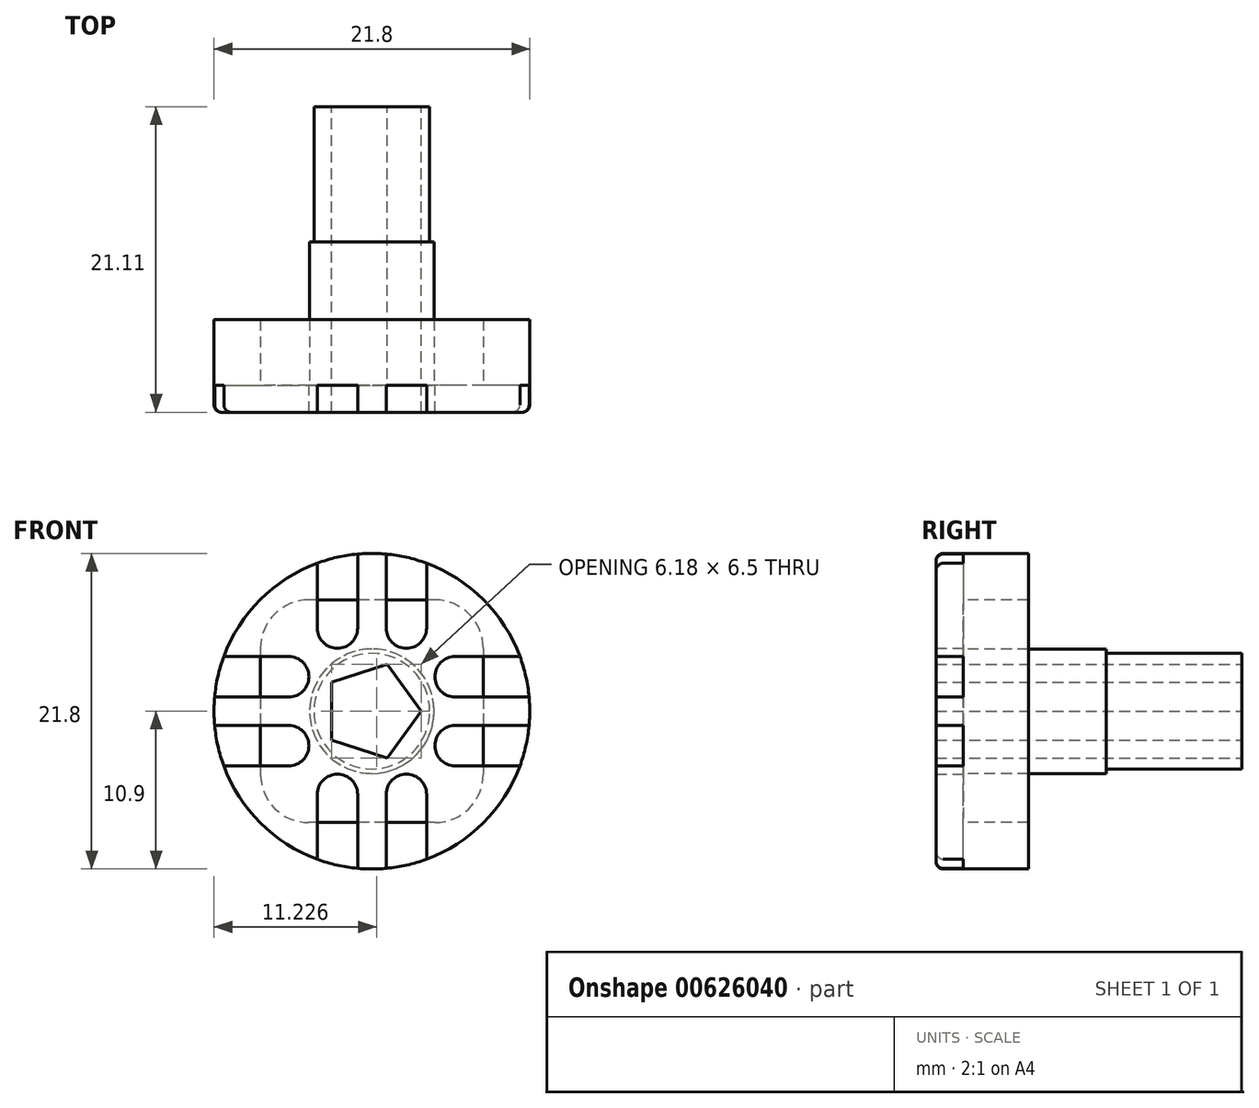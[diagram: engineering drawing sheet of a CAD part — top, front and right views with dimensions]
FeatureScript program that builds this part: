
annotation { "Feature Type Name" : "Feature", "Feature Type Description" : "" }
export const myFeature = defineFeature(function(context is Context, id is Id, definition is map)
    precondition{}
    {
        {
            var Q0;
            Q0=qCreatedBy(makeId("Front.planeOp"),FACE);
            var sketch = newSketch(context, id + "F0", { "sketchPlane" : qUnion([Q0])});
            skCircle(sketch, "E0", {"center": v(0, 0) * mm, "radius": 10.9 * mm});
            skLineSegment(sketch, "E1", {"start": v(-3.77, 10.23) * mm, "end": v(-3.77, 5.75) * mm});
            skLineSegment(sketch, "E2", {"start": v(-0.98, 10.86) * mm, "end": v(-0.98, 5.75) * mm});
            skLineSegment(sketch, "E3", {"start": v(0.99, 10.86) * mm, "end": v(0.99, 5.75) * mm});
            skLineSegment(sketch, "E4", {"start": v(3.78, 10.23) * mm, "end": v(3.78, 5.75) * mm});
            skLineSegment(sketch, "E5", {"start": v(-3.78, -10.23) * mm, "end": v(-3.78, -5.74) * mm});
            skLineSegment(sketch, "E6", {"start": v(-0.99, -10.86) * mm, "end": v(-0.99, -5.74) * mm});
            skLineSegment(sketch, "E7", {"start": v(0.99, -10.86) * mm, "end": v(0.99, -5.74) * mm});
            skLineSegment(sketch, "E8", {"start": v(3.78, -10.23) * mm, "end": v(3.78, -5.74) * mm});
            skLineSegment(sketch, "E9", {"start": v(10.23, -3.78) * mm, "end": v(5.75, -3.78) * mm});
            skLineSegment(sketch, "E10", {"start": v(10.23, 3.78) * mm, "end": v(5.75, 3.78) * mm});
            skLineSegment(sketch, "E11", {"start": v(10.86, 0.99) * mm, "end": v(5.75, 0.99) * mm});
            skLineSegment(sketch, "E12", {"start": v(10.86, -0.99) * mm, "end": v(5.75, -0.99) * mm});
            skLineSegment(sketch, "E13", {"start": v(-10.23, 3.78) * mm, "end": v(-5.75, 3.78) * mm});
            skLineSegment(sketch, "E14", {"start": v(-10.86, 0.99) * mm, "end": v(-5.75, 0.99) * mm});
            skLineSegment(sketch, "E15", {"start": v(-10.86, -0.98) * mm, "end": v(-5.75, -0.98) * mm});
            skLineSegment(sketch, "E16", {"start": v(-10.23, -3.78) * mm, "end": v(-5.75, -3.78) * mm});
            skLineSegment(sketch, "E17", {"start": v(-5.75, -0.98) * mm, "end": v(-5.75, -3.78) * mm, "construction": true});
            skLineSegment(sketch, "E18", {"start": v(-0.98, 5.75) * mm, "end": v(-3.77, 5.75) * mm, "construction": true});
            skLineSegment(sketch, "E19", {"start": v(-0.99, -5.74) * mm, "end": v(-3.78, -5.74) * mm, "construction": true});
            skLineSegment(sketch, "E20", {"start": v(0.99, -5.74) * mm, "end": v(3.78, -5.74) * mm, "construction": true});
            skLineSegment(sketch, "E21", {"start": v(5.75, -0.99) * mm, "end": v(5.75, -3.78) * mm, "construction": true});
            skLineSegment(sketch, "E22", {"start": v(5.75, 0.99) * mm, "end": v(5.75, 3.78) * mm, "construction": true});
            skLineSegment(sketch, "E23", {"start": v(0.99, 5.75) * mm, "end": v(3.78, 5.75) * mm, "construction": true});
            skLineSegment(sketch, "E24", {"start": v(-5.75, 3.78) * mm, "end": v(-5.75, 0.98) * mm, "construction": true});
            skArc(sketch, "E25", {"start": v(-5.75, -3.78) * mm, "mid": v(-4.35, -2.38) * mm, "end": v(-5.75, -0.98) * mm});
            skArc(sketch, "E26", {"start": v(-5.75, 0.99) * mm, "mid": v(-4.35, 2.38) * mm, "end": v(-5.75, 3.78) * mm});
            skArc(sketch, "E27", {"start": v(3.78, -5.74) * mm, "mid": v(2.38, -4.35) * mm, "end": v(0.99, -5.74) * mm});
            skArc(sketch, "E28", {"start": v(-0.99, -5.74) * mm, "mid": v(-2.38, -4.35) * mm, "end": v(-3.78, -5.74) * mm});
            skArc(sketch, "E29", {"start": v(5.75, 3.78) * mm, "mid": v(4.35, 2.38) * mm, "end": v(5.75, 0.99) * mm});
            skArc(sketch, "E30", {"start": v(5.75, -0.99) * mm, "mid": v(4.35, -2.38) * mm, "end": v(5.75, -3.78) * mm});
            skArc(sketch, "E31", {"start": v(-3.77, 5.75) * mm, "mid": v(-2.38, 4.35) * mm, "end": v(-0.98, 5.75) * mm});
            skArc(sketch, "E32", {"start": v(0.99, 5.75) * mm, "mid": v(2.38, 4.35) * mm, "end": v(3.78, 5.75) * mm});
            skLineSegment(sketch, "E33", {"start": v(-4.35, 2.38) * mm, "end": v(4.35, 2.38) * mm, "construction": true});
            skCircle(sketch, "E34.cCircle", {"center": v(0, 0) * mm, "radius": 2.76 * mm, "construction": true});
            skLineSegment(sketch, "E34.0", {"start": v(-2.76, -2) * mm, "end": v(-2.76, 2) * mm});
            skLineSegment(sketch, "E34.1", {"start": v(-2.76, 2) * mm, "end": v(1.06, 3.25) * mm});
            skLineSegment(sketch, "E34.2", {"start": v(1.06, 3.25) * mm, "end": v(3.42, 0) * mm});
            skLineSegment(sketch, "E34.3", {"start": v(3.42, 0) * mm, "end": v(1.06, -3.25) * mm});
            skLineSegment(sketch, "E34.4", {"start": v(1.06, -3.25) * mm, "end": v(-2.76, -2) * mm});
            skPoint(sketch, "E34.0.midPoint", {"position": v(-2.76, 0) * mm});
            skSolve(sketch);
        }
        {
            var Q0;
            {var subQ12=sQuery(id+"F0.wireOp",EDGE,"E1");Q0=makeQuery(id+"F0.imprint","IMPRINT",FACE,{"disambiguationData":[TD([[makeQuery(id+"F0.imprint","IMPRINT",EDGE,{"derivedFrom":subQ12}),-1.0]])]});}
            extrude(context, id + "F1", {"entities" : qUnion([Q0]), "depth" : 1.87 * mm, "offsetDistance" : 25 * mm});
        }
        {
            var Q0;
            Q0=makeQuery(id+"F1.opExtrude","CAP_FACE",FACE,{"disambiguationData":[OSD([sQuery(id+"F0.wireOp",EDGE,"E0"),sQuery(id+"F0.wireOp",EDGE,"E1"),sQuery(id+"F0.wireOp",EDGE,"E2"),sQuery(id+"F0.wireOp",EDGE,"E3"),sQuery(id+"F0.wireOp",EDGE,"E4"),sQuery(id+"F0.wireOp",EDGE,"E5"),sQuery(id+"F0.wireOp",EDGE,"E6"),sQuery(id+"F0.wireOp",EDGE,"E7"),sQuery(id+"F0.wireOp",EDGE,"E8"),sQuery(id+"F0.wireOp",EDGE,"E9"),sQuery(id+"F0.wireOp",EDGE,"E10"),sQuery(id+"F0.wireOp",EDGE,"E11"),sQuery(id+"F0.wireOp",EDGE,"E12"),sQuery(id+"F0.wireOp",EDGE,"E13"),sQuery(id+"F0.wireOp",EDGE,"E14"),sQuery(id+"F0.wireOp",EDGE,"E15"),sQuery(id+"F0.wireOp",EDGE,"E16"),sQuery(id+"F0.wireOp",EDGE,"E25"),sQuery(id+"F0.wireOp",EDGE,"E26"),sQuery(id+"F0.wireOp",EDGE,"E27"),sQuery(id+"F0.wireOp",EDGE,"E28"),sQuery(id+"F0.wireOp",EDGE,"E29"),sQuery(id+"F0.wireOp",EDGE,"E30"),sQuery(id+"F0.wireOp",EDGE,"E31"),sQuery(id+"F0.wireOp",EDGE,"E32"),sQuery(id+"F0.wireOp",EDGE,"E34.0"),sQuery(id+"F0.wireOp",EDGE,"E34.1"),sQuery(id+"F0.wireOp",EDGE,"E34.2"),sQuery(id+"F0.wireOp",EDGE,"E34.3"),sQuery(id+"F0.wireOp",EDGE,"E34.4")])],"isStart":true});
            var sketch = newSketch(context, id + "F2", { "sketchPlane" : qUnion([Q0])});
            skCircle(sketch, "E35", {"center": v(0, 0) * mm, "radius": 4.3 * mm});
            skSolve(sketch);
        }
        {
            var Q0;
            Q0=makeQuery(id+"F2.imprint","IMPRINT",FACE,{"disambiguationData":[TD([[makeQuery(id+"F2.imprint","IMPRINT",EDGE,{"derivedFrom":sQuery(id+"F2.wireOp",EDGE,"E35")}),1.0]])]});
            extrude(context, id + "F3", {"entities" : qUnion([Q0]), "operationType" : NewBodyOperationType.ADD, "depth" : 9.9 * mm, "offsetDistance" : 25 * mm});
        }
        {
            var Q0;
            Q0=makeQuery(id+"F3.opExtrude","CAP_FACE",FACE,{"disambiguationData":[OSD([sQuery(id+"F0.wireOp",EDGE,"E34.0"),sQuery(id+"F0.wireOp",EDGE,"E34.1"),sQuery(id+"F0.wireOp",EDGE,"E34.2"),sQuery(id+"F0.wireOp",EDGE,"E34.3"),sQuery(id+"F0.wireOp",EDGE,"E34.4"),sQuery(id+"F2.wireOp",EDGE,"E35")])],"isStart":false});
            var sketch = newSketch(context, id + "F4", { "sketchPlane" : qUnion([Q0])});
            skCircle(sketch, "E36", {"center": v(0, 0) * mm, "radius": 4 * mm});
            skSolve(sketch);
        }
        {
            var Q0;
            Q0=makeQuery(id+"F4.imprint","IMPRINT",FACE,{"disambiguationData":[TD([[makeQuery(id+"F4.imprint","IMPRINT",EDGE,{"derivedFrom":sQuery(id+"F4.wireOp",EDGE,"E36")}),1.0]])]});
            extrude(context, id + "F5", {"entities" : qUnion([Q0]), "operationType" : NewBodyOperationType.ADD, "depth" : 9.35 * mm, "offsetDistance" : 25 * mm});
        }
        {
            var Q0;
            Q0=makeQuery(id+"F1.opExtrude","CAP_FACE",FACE,{"disambiguationData":[OSD([sQuery(id+"F0.wireOp",EDGE,"E0"),sQuery(id+"F0.wireOp",EDGE,"E1"),sQuery(id+"F0.wireOp",EDGE,"E2"),sQuery(id+"F0.wireOp",EDGE,"E3"),sQuery(id+"F0.wireOp",EDGE,"E4"),sQuery(id+"F0.wireOp",EDGE,"E5"),sQuery(id+"F0.wireOp",EDGE,"E6"),sQuery(id+"F0.wireOp",EDGE,"E7"),sQuery(id+"F0.wireOp",EDGE,"E8"),sQuery(id+"F0.wireOp",EDGE,"E9"),sQuery(id+"F0.wireOp",EDGE,"E10"),sQuery(id+"F0.wireOp",EDGE,"E11"),sQuery(id+"F0.wireOp",EDGE,"E12"),sQuery(id+"F0.wireOp",EDGE,"E13"),sQuery(id+"F0.wireOp",EDGE,"E14"),sQuery(id+"F0.wireOp",EDGE,"E15"),sQuery(id+"F0.wireOp",EDGE,"E16"),sQuery(id+"F0.wireOp",EDGE,"E25"),sQuery(id+"F0.wireOp",EDGE,"E26"),sQuery(id+"F0.wireOp",EDGE,"E27"),sQuery(id+"F0.wireOp",EDGE,"E28"),sQuery(id+"F0.wireOp",EDGE,"E29"),sQuery(id+"F0.wireOp",EDGE,"E30"),sQuery(id+"F0.wireOp",EDGE,"E31"),sQuery(id+"F0.wireOp",EDGE,"E32"),sQuery(id+"F0.wireOp",EDGE,"E34.0"),sQuery(id+"F0.wireOp",EDGE,"E34.1"),sQuery(id+"F0.wireOp",EDGE,"E34.2"),sQuery(id+"F0.wireOp",EDGE,"E34.3"),sQuery(id+"F0.wireOp",EDGE,"E34.4")])],"isStart":true});
            var sketch = newSketch(context, id + "F6", { "sketchPlane" : qUnion([Q0])});
            skLineSegment(sketch, "E37.bottom", {"start": v(-7.7, 7.69) * mm, "end": v(7.69, 7.69) * mm});
            skLineSegment(sketch, "E37.top", {"start": v(-7.69, -7.7) * mm, "end": v(7.7, -7.7) * mm});
            skLineSegment(sketch, "E37.left", {"start": v(-7.7, 7.69) * mm, "end": v(-7.69, -7.7) * mm});
            skLineSegment(sketch, "E37.right", {"start": v(7.69, 7.69) * mm, "end": v(7.69, -7.7) * mm});
            skPoint(sketch, "E37.middle", {"position": v(0, 0) * mm});
            skArc(sketch, "E38", {"start": v(-4.36, 7.69) * mm, "mid": v(-6.71, 6.71) * mm, "end": v(-7.7, 4.36) * mm});
            skArc(sketch, "E39", {"start": v(7.69, 4.36) * mm, "mid": v(6.71, 6.71) * mm, "end": v(4.36, 7.69) * mm});
            skArc(sketch, "E40", {"start": v(4.36, -7.7) * mm, "mid": v(6.71, -6.71) * mm, "end": v(7.7, -4.36) * mm});
            skArc(sketch, "E41", {"start": v(-7.69, -4.36) * mm, "mid": v(-6.71, -6.71) * mm, "end": v(-4.36, -7.7) * mm});
            skPoint(sketch, "E42.0", {"position": v(0, 10.9) * mm});
            skCircle(sketch, "E43", {"center": v(0, 0) * mm, "radius": 10.9 * mm});
            skSolve(sketch);
        }
        {
            var Q0;
            {var subQ0=sQuery(id+"F6.wireOp",EDGE,"E37.left");var subQ1=sQuery(id+"F6.wireOp",EDGE,"E37.bottom");var subQ2=makeQuery(id+"F6.imprint","INTERSECT",VERTEX,{"derivedFrom":[subQ1,subQ0]});Q0=makeQuery(id+"F6.imprint","IMPRINT",FACE,{"disambiguationData":[TD([[makeQuery(id+"F6.imprint","IMPRINT",EDGE,{"disambiguationData":[TD([[subQ2,-1.0]])],"derivedFrom":subQ1}),1.0]])]});}
            var Q1;
            {var subQ3=sQuery(id+"F6.wireOp",EDGE,"E38");Q1=makeQuery(id+"F6.imprint","IMPRINT",FACE,{"disambiguationData":[TD([[makeQuery(id+"F6.imprint","IMPRINT",EDGE,{"derivedFrom":subQ3}),-1.0]])]});}
            var Q2;
            {var subQ0=sQuery(id+"F6.wireOp",EDGE,"E39");var subQ5=sQuery(id+"F6.wireOp",EDGE,"E37.bottom");var subQ7=makeQuery(id+"F6.imprint","INTERSECT",VERTEX,{"derivedFrom":[subQ5,subQ0]});Q2=makeQuery(id+"F6.imprint","IMPRINT",FACE,{"disambiguationData":[TD([[makeQuery(id+"F6.imprint","IMPRINT",EDGE,{"disambiguationData":[TD([[subQ7,1.0]])],"derivedFrom":subQ5}),1.0]])]});}
            var Q3;
            {var subQ3=sQuery(id+"F6.wireOp",EDGE,"E39");Q3=makeQuery(id+"F6.imprint","IMPRINT",FACE,{"disambiguationData":[TD([[makeQuery(id+"F6.imprint","IMPRINT",EDGE,{"derivedFrom":subQ3}),-1.0]])]});}
            var Q4;
            {var subQ0=sQuery(id+"F6.wireOp",EDGE,"E37.right");var subQ1=makeQuery(id+"F1.opExtrude","CAP_EDGE",EDGE,{"disambiguationData":[OSD([sQuery(id+"F0.wireOp",EDGE,"E13")])],"isStart":true});var subQ2=makeQuery(id+"F6.imprint","INTERSECT",VERTEX,{"derivedFrom":[subQ1,subQ0]});Q4=makeQuery(id+"F6.imprint","IMPRINT",FACE,{"disambiguationData":[TD([[makeQuery(id+"F6.imprint","IMPRINT",EDGE,{"disambiguationData":[TD([[subQ2,-1.0]])],"derivedFrom":subQ0}),1.0]])]});}
            var Q5;
            {var subQ0=sQuery(id+"F6.wireOp",EDGE,"E37.right");var subQ1=makeQuery(id+"F1.opExtrude","CAP_EDGE",EDGE,{"disambiguationData":[OSD([sQuery(id+"F0.wireOp",EDGE,"E14")])],"isStart":true});var subQ2=makeQuery(id+"F6.imprint","INTERSECT",VERTEX,{"derivedFrom":[subQ1,subQ0]});Q5=makeQuery(id+"F6.imprint","IMPRINT",FACE,{"disambiguationData":[TD([[makeQuery(id+"F6.imprint","IMPRINT",EDGE,{"disambiguationData":[TD([[subQ2,-1.0]])],"derivedFrom":subQ0}),1.0]])]});}
            var Q6;
            {var subQ0=sQuery(id+"F6.wireOp",EDGE,"E37.right");var subQ1=makeQuery(id+"F1.opExtrude","CAP_EDGE",EDGE,{"disambiguationData":[OSD([sQuery(id+"F0.wireOp",EDGE,"E15")])],"isStart":true});var subQ2=makeQuery(id+"F6.imprint","INTERSECT",VERTEX,{"derivedFrom":[subQ1,subQ0]});Q6=makeQuery(id+"F6.imprint","IMPRINT",FACE,{"disambiguationData":[TD([[makeQuery(id+"F6.imprint","IMPRINT",EDGE,{"disambiguationData":[TD([[subQ2,-1.0]])],"derivedFrom":subQ0}),1.0]])]});}
            var Q7;
            {var subQ0=sQuery(id+"F6.wireOp",EDGE,"E40");var subQ5=sQuery(id+"F6.wireOp",EDGE,"E37.top");var subQ7=makeQuery(id+"F6.imprint","INTERSECT",VERTEX,{"derivedFrom":[subQ5,subQ0]});Q7=makeQuery(id+"F6.imprint","IMPRINT",FACE,{"disambiguationData":[TD([[makeQuery(id+"F6.imprint","IMPRINT",EDGE,{"disambiguationData":[TD([[subQ7,1.0]])],"derivedFrom":subQ5}),-1.0]])]});}
            var Q8;
            {var subQ3=sQuery(id+"F6.wireOp",EDGE,"E40");Q8=makeQuery(id+"F6.imprint","IMPRINT",FACE,{"disambiguationData":[TD([[makeQuery(id+"F6.imprint","IMPRINT",EDGE,{"derivedFrom":subQ3}),-1.0]])]});}
            var Q9;
            {var subQ0=sQuery(id+"F6.wireOp",EDGE,"E37.top");var subQ1=makeQuery(id+"F1.opExtrude","CAP_EDGE",EDGE,{"disambiguationData":[OSD([sQuery(id+"F0.wireOp",EDGE,"E6")])],"isStart":true});var subQ2=makeQuery(id+"F6.imprint","INTERSECT",VERTEX,{"derivedFrom":[subQ1,subQ0]});Q9=makeQuery(id+"F6.imprint","IMPRINT",FACE,{"disambiguationData":[TD([[makeQuery(id+"F6.imprint","IMPRINT",EDGE,{"disambiguationData":[TD([[subQ2,-1.0]])],"derivedFrom":subQ0}),-1.0]])]});}
            var Q10;
            {var subQ0=sQuery(id+"F6.wireOp",EDGE,"E37.top");var subQ1=makeQuery(id+"F1.opExtrude","CAP_EDGE",EDGE,{"disambiguationData":[OSD([sQuery(id+"F0.wireOp",EDGE,"E7")])],"isStart":true});var subQ2=makeQuery(id+"F6.imprint","INTERSECT",VERTEX,{"derivedFrom":[subQ1,subQ0]});Q10=makeQuery(id+"F6.imprint","IMPRINT",FACE,{"disambiguationData":[TD([[makeQuery(id+"F6.imprint","IMPRINT",EDGE,{"disambiguationData":[TD([[subQ2,-1.0]])],"derivedFrom":subQ0}),-1.0]])]});}
            var Q11;
            {var subQ0=sQuery(id+"F6.wireOp",EDGE,"E37.top");var subQ1=makeQuery(id+"F1.opExtrude","CAP_EDGE",EDGE,{"disambiguationData":[OSD([sQuery(id+"F0.wireOp",EDGE,"E8")])],"isStart":true});var subQ2=makeQuery(id+"F6.imprint","INTERSECT",VERTEX,{"derivedFrom":[subQ1,subQ0]});Q11=makeQuery(id+"F6.imprint","IMPRINT",FACE,{"disambiguationData":[TD([[makeQuery(id+"F6.imprint","IMPRINT",EDGE,{"disambiguationData":[TD([[subQ2,-1.0]])],"derivedFrom":subQ0}),-1.0]])]});}
            var Q12;
            {var subQ0=sQuery(id+"F6.wireOp",EDGE,"E37.left");var subQ1=sQuery(id+"F6.wireOp",EDGE,"E37.top");var subQ2=makeQuery(id+"F6.imprint","INTERSECT",VERTEX,{"derivedFrom":[subQ1,subQ0]});Q12=makeQuery(id+"F6.imprint","IMPRINT",FACE,{"disambiguationData":[TD([[makeQuery(id+"F6.imprint","IMPRINT",EDGE,{"disambiguationData":[TD([[subQ2,-1.0]])],"derivedFrom":subQ1}),-1.0]])]});}
            var Q13;
            {var subQ3=sQuery(id+"F6.wireOp",EDGE,"E41");Q13=makeQuery(id+"F6.imprint","IMPRINT",FACE,{"disambiguationData":[TD([[makeQuery(id+"F6.imprint","IMPRINT",EDGE,{"derivedFrom":subQ3}),-1.0]])]});}
            var Q14;
            {var subQ0=sQuery(id+"F6.wireOp",EDGE,"E37.left");var subQ1=makeQuery(id+"F1.opExtrude","CAP_EDGE",EDGE,{"disambiguationData":[OSD([sQuery(id+"F0.wireOp",EDGE,"E12")])],"isStart":true});var subQ2=makeQuery(id+"F6.imprint","INTERSECT",VERTEX,{"derivedFrom":[subQ1,subQ0]});Q14=makeQuery(id+"F6.imprint","IMPRINT",FACE,{"disambiguationData":[TD([[makeQuery(id+"F6.imprint","IMPRINT",EDGE,{"disambiguationData":[TD([[subQ2,-1.0]])],"derivedFrom":subQ0}),-1.0]])]});}
            var Q15;
            {var subQ0=sQuery(id+"F6.wireOp",EDGE,"E37.left");var subQ1=makeQuery(id+"F1.opExtrude","CAP_EDGE",EDGE,{"disambiguationData":[OSD([sQuery(id+"F0.wireOp",EDGE,"E11")])],"isStart":true});var subQ2=makeQuery(id+"F6.imprint","INTERSECT",VERTEX,{"derivedFrom":[subQ1,subQ0]});Q15=makeQuery(id+"F6.imprint","IMPRINT",FACE,{"disambiguationData":[TD([[makeQuery(id+"F6.imprint","IMPRINT",EDGE,{"disambiguationData":[TD([[subQ2,-1.0]])],"derivedFrom":subQ0}),-1.0]])]});}
            var Q16;
            {var subQ0=sQuery(id+"F6.wireOp",EDGE,"E37.left");var subQ1=makeQuery(id+"F1.opExtrude","CAP_EDGE",EDGE,{"disambiguationData":[OSD([sQuery(id+"F0.wireOp",EDGE,"E10")])],"isStart":true});var subQ2=makeQuery(id+"F6.imprint","INTERSECT",VERTEX,{"derivedFrom":[subQ1,subQ0]});Q16=makeQuery(id+"F6.imprint","IMPRINT",FACE,{"disambiguationData":[TD([[makeQuery(id+"F6.imprint","IMPRINT",EDGE,{"disambiguationData":[TD([[subQ2,-1.0]])],"derivedFrom":subQ0}),-1.0]])]});}
            var Q17;
            {var subQ0=sQuery(id+"F6.wireOp",EDGE,"E37.bottom");var subQ1=makeQuery(id+"F1.opExtrude","CAP_EDGE",EDGE,{"disambiguationData":[OSD([sQuery(id+"F0.wireOp",EDGE,"E4")])],"isStart":true});var subQ2=makeQuery(id+"F6.imprint","INTERSECT",VERTEX,{"derivedFrom":[subQ1,subQ0]});Q17=makeQuery(id+"F6.imprint","IMPRINT",FACE,{"disambiguationData":[TD([[makeQuery(id+"F6.imprint","IMPRINT",EDGE,{"disambiguationData":[TD([[subQ2,-1.0]])],"derivedFrom":subQ0}),1.0]])]});}
            var Q18;
            {var subQ0=sQuery(id+"F6.wireOp",EDGE,"E37.bottom");var subQ1=makeQuery(id+"F1.opExtrude","CAP_EDGE",EDGE,{"disambiguationData":[OSD([sQuery(id+"F0.wireOp",EDGE,"E3")])],"isStart":true});var subQ2=makeQuery(id+"F6.imprint","INTERSECT",VERTEX,{"derivedFrom":[subQ1,subQ0]});Q18=makeQuery(id+"F6.imprint","IMPRINT",FACE,{"disambiguationData":[TD([[makeQuery(id+"F6.imprint","IMPRINT",EDGE,{"disambiguationData":[TD([[subQ2,-1.0]])],"derivedFrom":subQ0}),1.0]])]});}
            var Q19;
            {var subQ0=sQuery(id+"F6.wireOp",EDGE,"E37.bottom");var subQ1=makeQuery(id+"F1.opExtrude","CAP_EDGE",EDGE,{"disambiguationData":[OSD([sQuery(id+"F0.wireOp",EDGE,"E2")])],"isStart":true});var subQ2=makeQuery(id+"F6.imprint","INTERSECT",VERTEX,{"derivedFrom":[subQ1,subQ0]});Q19=makeQuery(id+"F6.imprint","IMPRINT",FACE,{"disambiguationData":[TD([[makeQuery(id+"F6.imprint","IMPRINT",EDGE,{"disambiguationData":[TD([[subQ2,-1.0]])],"derivedFrom":subQ0}),1.0]])]});}
            extrude(context, id + "F7", {"entities" : qUnion([Q0, Q1, Q2, Q3, Q4, Q5, Q6, Q7, Q8, Q9, Q10, Q11, Q12, Q13, Q14, Q15, Q16, Q17, Q18, Q19]), "operationType" : NewBodyOperationType.ADD, "depth" : 4.52 * mm, "offsetDistance" : 25 * mm});
        }
        {
            var Q0;
            {var subQ0=sQuery(id+"F0.wireOp",EDGE,"E0");Q0=makeQuery(id+"F1.opExtrude","CAP_EDGE",EDGE,{"disambiguationData":[OSD([subQ0]),TDD([makeQuery(id+"F0.imprint","IMPRINT",EDGE,{"disambiguationData":[TD([[makeQuery(id+"F0.imprint","INTERSECT",VERTEX,{"derivedFrom":[subQ0,sQuery(id+"F0.wireOp",EDGE,"E8")]}),-1.0]])],"derivedFrom":subQ0})])],"isStart":false});}
            var Q1;
            {var subQ0=sQuery(id+"F0.wireOp",EDGE,"E0");Q1=makeQuery(id+"F1.opExtrude","CAP_EDGE",EDGE,{"disambiguationData":[OSD([subQ0]),TDD([makeQuery(id+"F0.imprint","IMPRINT",EDGE,{"disambiguationData":[TD([[makeQuery(id+"F0.imprint","INTERSECT",VERTEX,{"derivedFrom":[subQ0,sQuery(id+"F0.wireOp",EDGE,"E6")]}),-1.0]])],"derivedFrom":subQ0})])],"isStart":false});}
            var Q2;
            {var subQ0=sQuery(id+"F0.wireOp",EDGE,"E0");Q2=makeQuery(id+"F1.opExtrude","CAP_EDGE",EDGE,{"disambiguationData":[OSD([subQ0]),TDD([makeQuery(id+"F0.imprint","IMPRINT",EDGE,{"disambiguationData":[TD([[makeQuery(id+"F0.imprint","INTERSECT",VERTEX,{"derivedFrom":[subQ0,sQuery(id+"F0.wireOp",EDGE,"E5")]}),1.0]])],"derivedFrom":subQ0})])],"isStart":false});}
            var Q3;
            {var subQ0=sQuery(id+"F0.wireOp",EDGE,"E0");Q3=makeQuery(id+"F1.opExtrude","CAP_EDGE",EDGE,{"disambiguationData":[OSD([subQ0]),TDD([makeQuery(id+"F0.imprint","IMPRINT",EDGE,{"disambiguationData":[TD([[makeQuery(id+"F0.imprint","INTERSECT",VERTEX,{"derivedFrom":[subQ0,sQuery(id+"F0.wireOp",EDGE,"E14")]}),-1.0]])],"derivedFrom":subQ0})])],"isStart":false});}
            var Q4;
            {var subQ0=sQuery(id+"F0.wireOp",EDGE,"E0");Q4=makeQuery(id+"F1.opExtrude","CAP_EDGE",EDGE,{"disambiguationData":[OSD([subQ0]),TDD([makeQuery(id+"F0.imprint","IMPRINT",EDGE,{"disambiguationData":[TD([[makeQuery(id+"F0.imprint","INTERSECT",VERTEX,{"derivedFrom":[subQ0,sQuery(id+"F0.wireOp",EDGE,"E1")]}),-1.0]])],"derivedFrom":subQ0})])],"isStart":false});}
            var Q5;
            {var subQ0=sQuery(id+"F0.wireOp",EDGE,"E0");Q5=makeQuery(id+"F1.opExtrude","CAP_EDGE",EDGE,{"disambiguationData":[OSD([subQ0]),TDD([makeQuery(id+"F0.imprint","IMPRINT",EDGE,{"disambiguationData":[TD([[makeQuery(id+"F0.imprint","INTERSECT",VERTEX,{"derivedFrom":[subQ0,sQuery(id+"F0.wireOp",EDGE,"E2")]}),1.0]])],"derivedFrom":subQ0})])],"isStart":false});}
            var Q6;
            {var subQ0=sQuery(id+"F0.wireOp",EDGE,"E0");Q6=makeQuery(id+"F1.opExtrude","CAP_EDGE",EDGE,{"disambiguationData":[OSD([subQ0]),TDD([makeQuery(id+"F0.imprint","IMPRINT",EDGE,{"disambiguationData":[TD([[makeQuery(id+"F0.imprint","INTERSECT",VERTEX,{"derivedFrom":[subQ0,sQuery(id+"F0.wireOp",EDGE,"E4")]}),1.0]])],"derivedFrom":subQ0})])],"isStart":false});}
            var Q7;
            {var subQ0=sQuery(id+"F0.wireOp",EDGE,"E0");Q7=makeQuery(id+"F1.opExtrude","CAP_EDGE",EDGE,{"disambiguationData":[OSD([subQ0]),TDD([makeQuery(id+"F0.imprint","IMPRINT",EDGE,{"disambiguationData":[TD([[makeQuery(id+"F0.imprint","INTERSECT",VERTEX,{"derivedFrom":[subQ0,sQuery(id+"F0.wireOp",EDGE,"E11")]}),1.0]])],"derivedFrom":subQ0})])],"isStart":false});}
            fillet(context, id + "F8", {"entities" : qUnion([Q0, Q1, Q2, Q3, Q4, Q5, Q6, Q7]), "radius" : 0.5 * mm, "tangentPropagation" : true, "allowEdgeOverflow" : false});
        }
    });
